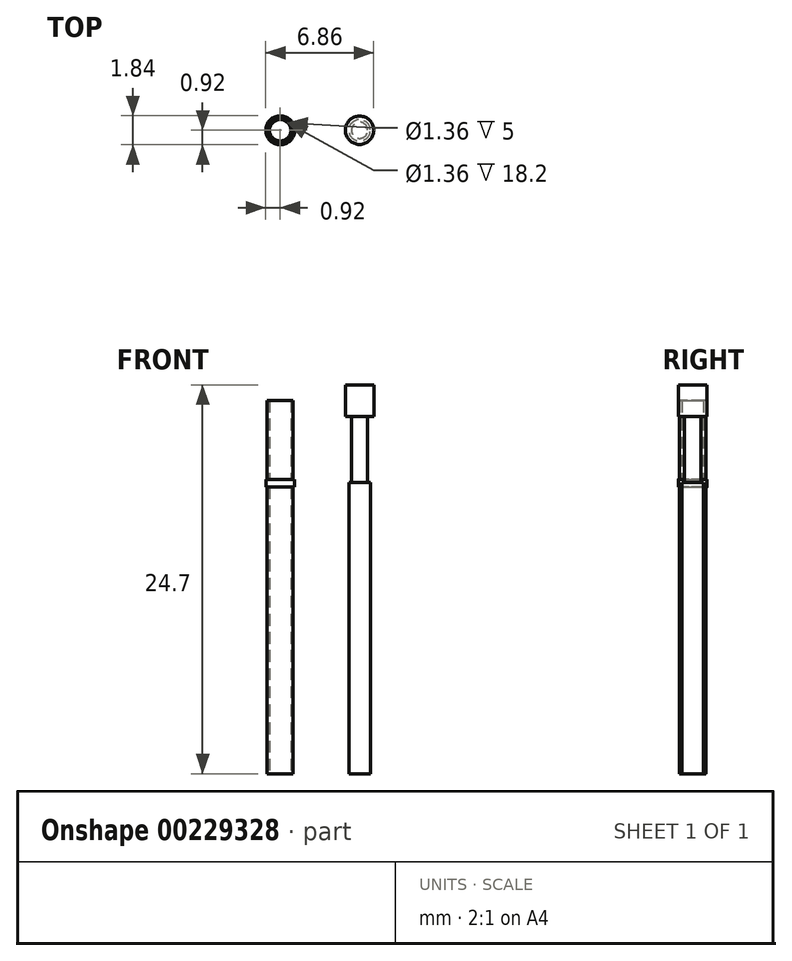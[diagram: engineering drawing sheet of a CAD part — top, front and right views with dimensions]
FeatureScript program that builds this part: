
annotation { "Feature Type Name" : "Feature", "Feature Type Description" : "" }
export const myFeature = defineFeature(function(context is Context, id is Id, definition is map)
    precondition{}
    {
        {
            var Q0;
            Q0=qCreatedBy(makeId("Top.planeOp"),FACE);
            var sketch = newSketch(context, id + "F0", { "sketchPlane" : qUnion([Q0])});
            skCircle(sketch, "E0", {"center": v(0, 0) * mm, "radius": 0.83 * mm});
            skCircle(sketch, "E1", {"center": v(0, 0) * mm, "radius": 0.68 * mm});
            skSolve(sketch);
        }
        {
            var Q0;
            Q0 = qSketchRegion(id + "F0", true);
            extrude(context, id + "F1", {"entities" : qUnion([Q0]), "depth" : 23.7 * mm});
        }
        {
            var Q0;
            Q0=qCreatedBy(makeId("Top.planeOp"),FACE);
            var sketch = newSketch(context, id + "F2", { "sketchPlane" : qUnion([Q0])});
            skCircle(sketch, "E2", {"center": v(5.04, 0) * mm, "radius": 0.68 * mm});
            skSolve(sketch);
        }
        {
            var Q0;
            Q0 = qSketchRegion(id + "F2", true);
            extrude(context, id + "F3", {"entities" : qUnion([Q0]), "depth" : 18.5 * mm});
        }
        {
            var Q0;
            Q0=makeQuery(id+"F3.opExtrude","CAP_FACE",FACE,{"disambiguationData":[OSD([sQuery(id+"F2.wireOp",EDGE,"E2")])],"isStart":false});
            var sketch = newSketch(context, id + "F4", { "sketchPlane" : qUnion([Q0])});
            skCircle(sketch, "E3", {"center": v(5.04, 0) * mm, "radius": 0.52 * mm});
            skSolve(sketch);
        }
        {
            var Q0;
            Q0 = qSketchRegion(id + "F4", true);
            extrude(context, id + "F5", {"entities" : qUnion([Q0]), "operationType" : NewBodyOperationType.ADD, "depth" : 4.2 * mm});
        }
        {
            var Q0;
            Q0=makeQuery(id+"F5.opExtrude","CAP_FACE",FACE,{"disambiguationData":[OSD([sQuery(id+"F4.wireOp",EDGE,"E3")])],"isStart":false});
            var sketch = newSketch(context, id + "F6", { "sketchPlane" : qUnion([Q0])});
            skCircle(sketch, "E4", {"center": v(5.04, 0) * mm, "radius": 0.9 * mm});
            skSolve(sketch);
        }
        {
            var Q0;
            Q0 = qSketchRegion(id + "F6", true);
            extrude(context, id + "F7", {"entities" : qUnion([Q0]), "operationType" : NewBodyOperationType.ADD, "depth" : 2 * mm});
        }
        {
            var Q0;
            Q0=qCreatedBy(makeId("Front.planeOp"),FACE);
            var sketch = newSketch(context, id + "F8", { "sketchPlane" : qUnion([Q0])});
            skLineSegment(sketch, "E5.bottom", {"start": v(0, 18.7) * mm, "end": v(-0.92, 18.7) * mm});
            skLineSegment(sketch, "E5.top", {"start": v(0, 18.2) * mm, "end": v(-0.92, 18.2) * mm});
            skLineSegment(sketch, "E5.left", {"start": v(0, 18.7) * mm, "end": v(0, 18.2) * mm});
            skLineSegment(sketch, "E5.right", {"start": v(-0.91, 18.7) * mm, "end": v(-0.91, 18.2) * mm});
            skSolve(sketch);
        }
        {
            var Q0;
            Q0 = qSketchRegion(id + "F8", true);
            var Q1;
            Q1=sQuery(id+"F8.wireOp",EDGE,"E5.left");
            revolve(context, id + "F9", {"operationType" : NewBodyOperationType.ADD, "entities" : qUnion([Q0]), "axis" : qUnion([Q1]), "revolveType" : RevolveType.FULL});
        }
    });
